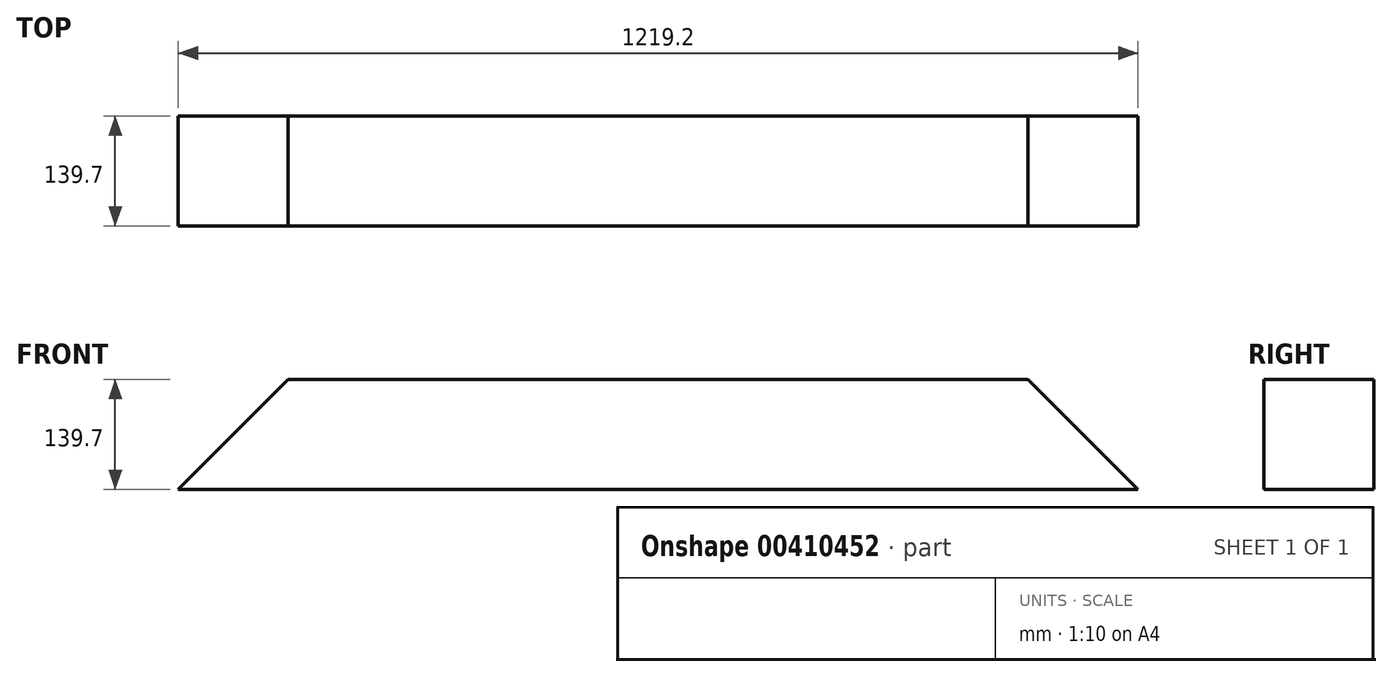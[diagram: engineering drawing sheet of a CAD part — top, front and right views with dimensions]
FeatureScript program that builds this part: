
annotation { "Feature Type Name" : "Feature", "Feature Type Description" : "" }
export const myFeature = defineFeature(function(context is Context, id is Id, definition is map)
    precondition{}
    {
        {
            var Q0;
            Q0=qCreatedBy(makeId("Front.planeOp"),FACE);
            var sketch = newSketch(context, id + "F0", { "sketchPlane" : qUnion([Q0])});
            skLineSegment(sketch, "E0.bottom", {"start": v(609.6, -69.85) * mm, "end": v(-609.6, -69.85) * mm});
            skLineSegment(sketch, "E0.top", {"start": v(609.6, 69.85) * mm, "end": v(-609.6, 69.85) * mm});
            skLineSegment(sketch, "E0.left", {"start": v(609.6, -69.85) * mm, "end": v(609.6, 69.85) * mm});
            skLineSegment(sketch, "E0.right", {"start": v(-609.6, -69.85) * mm, "end": v(-609.6, 69.85) * mm});
            skPoint(sketch, "E0.middle", {"position": v(0, 0) * mm});
            skLineSegment(sketch, "E1", {"start": v(-609.6, -69.85) * mm, "end": v(-469.9, 69.85) * mm});
            skLineSegment(sketch, "E2", {"start": v(609.6, -69.85) * mm, "end": v(469.9, 69.85) * mm});
            skSolve(sketch);
        }
        {
            var Q0;
            Q0=makeQuery(id+"F0.imprint","IMPRINT",FACE,{"disambiguationData":[TD([[makeQuery(id+"F0.imprint","IMPRINT",EDGE,{"derivedFrom":sQuery(id+"F0.wireOp",EDGE,"E0.bottom")}),-1.0]])]});
            extrude(context, id + "F1", {"entities" : qUnion([Q0]), "depth" : 139.7 * mm, "offsetDistance" : 25.4 * mm, "symmetric" : true});
        }
    });
